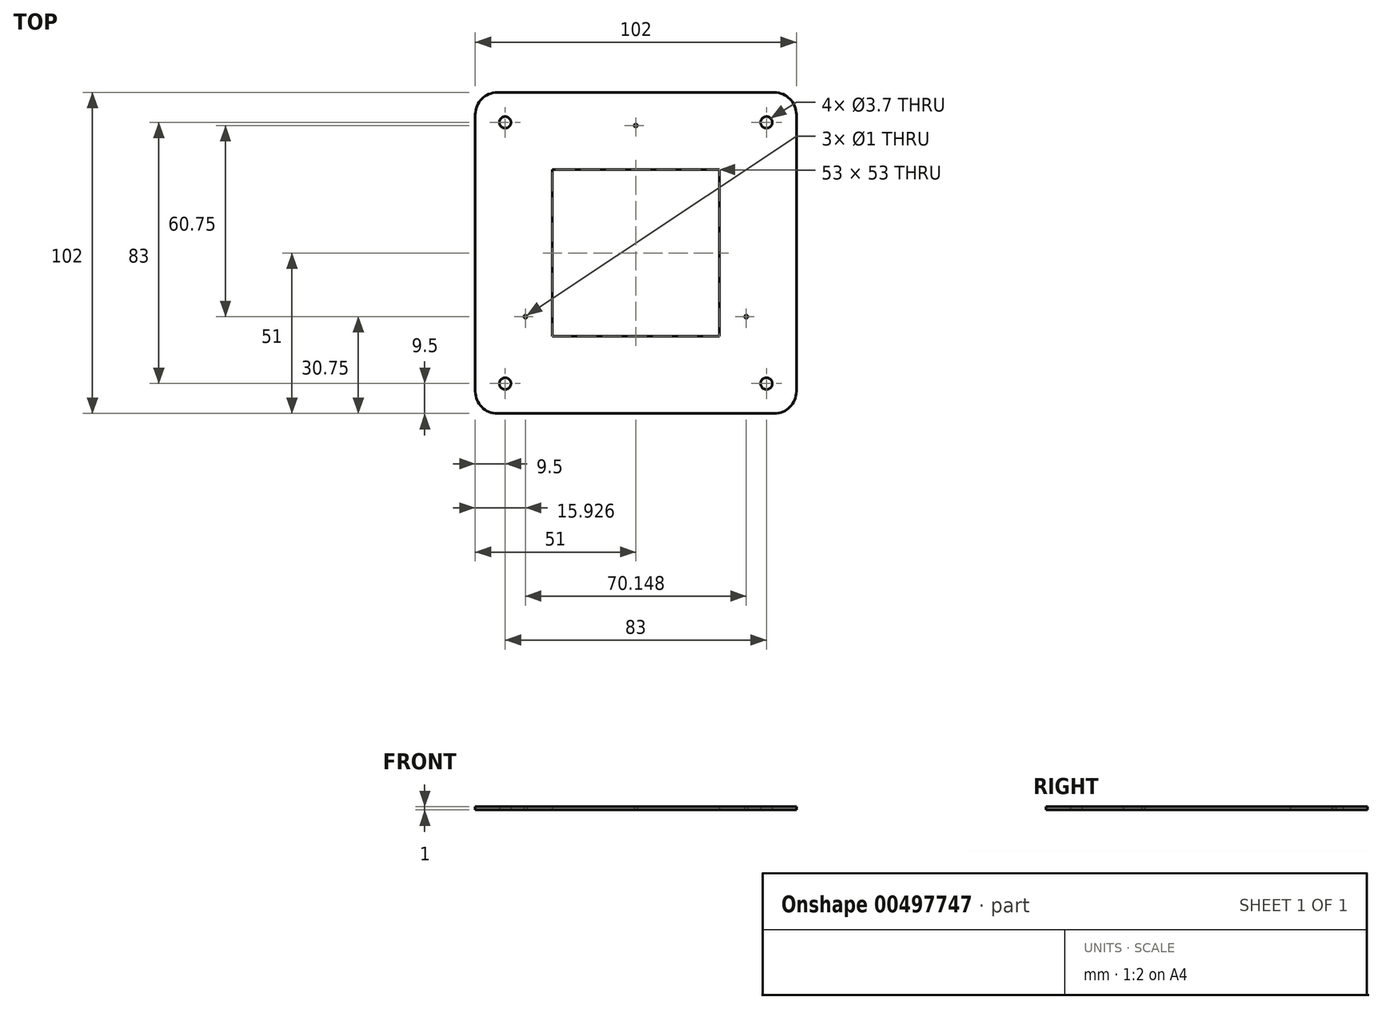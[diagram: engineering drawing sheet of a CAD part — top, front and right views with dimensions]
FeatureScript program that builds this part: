
annotation { "Feature Type Name" : "Feature", "Feature Type Description" : "" }
export const myFeature = defineFeature(function(context is Context, id is Id, definition is map)
    precondition{}
    {
        {
            var Q0;
            Q0=qCreatedBy(makeId("Top.planeOp"),FACE);
            var sketch = newSketch(context, id + "F0", { "sketchPlane" : qUnion([Q0])});
            skCircle(sketch, "E0", {"center": v(0, 0) * mm, "radius": 40.5 * mm, "construction": true});
            skLineSegment(sketch, "E1", {"start": v(0, 40.5) * mm, "end": v(-35.07, -20.25) * mm, "construction": true});
            skLineSegment(sketch, "E2", {"start": v(-35.07, -20.25) * mm, "end": v(35.07, -20.25) * mm, "construction": true});
            skLineSegment(sketch, "E3", {"start": v(35.07, -20.25) * mm, "end": v(0, 40.5) * mm, "construction": true});
            skCircle(sketch, "E4", {"center": v(-35.07, -20.25) * mm, "radius": 0.5 * mm});
            skCircle(sketch, "E5", {"center": v(35.07, -20.25) * mm, "radius": 0.5 * mm});
            skCircle(sketch, "E6", {"center": v(0, 40.5) * mm, "radius": 0.5 * mm});
            skLineSegment(sketch, "E7.bottom", {"start": v(44, -51) * mm, "end": v(-44, -51) * mm});
            skLineSegment(sketch, "E7.top", {"start": v(44, 51) * mm, "end": v(-44, 51) * mm});
            skLineSegment(sketch, "E7.left", {"start": v(51, -44) * mm, "end": v(51, 44) * mm});
            skLineSegment(sketch, "E7.right", {"start": v(-51, -44) * mm, "end": v(-51, 44) * mm});
            skLineSegment(sketch, "E8.bottom", {"start": v(41.5, 41.5) * mm, "end": v(-41.5, 41.5) * mm, "construction": true});
            skLineSegment(sketch, "E8.top", {"start": v(41.5, -41.5) * mm, "end": v(-41.5, -41.5) * mm, "construction": true});
            skLineSegment(sketch, "E8.left", {"start": v(41.5, 41.5) * mm, "end": v(41.5, -41.5) * mm, "construction": true});
            skLineSegment(sketch, "E8.right", {"start": v(-41.5, 41.5) * mm, "end": v(-41.5, -41.5) * mm, "construction": true});
            skCircle(sketch, "E9", {"center": v(-41.5, 41.5) * mm, "radius": 1.85 * mm});
            skCircle(sketch, "E10", {"center": v(41.5, 41.5) * mm, "radius": 1.85 * mm});
            skCircle(sketch, "E11", {"center": v(41.5, -41.5) * mm, "radius": 1.85 * mm});
            skCircle(sketch, "E12", {"center": v(-41.5, -41.5) * mm, "radius": 1.85 * mm});
            skPoint(sketch, "E13.visualSharp", {"position": v(-51, 51) * mm});
            skArc(sketch, "E13.filletArc", {"start": v(-44, 51) * mm, "mid": v(-48.95, 48.95) * mm, "end": v(-51, 44) * mm});
            skPoint(sketch, "E14.visualSharp", {"position": v(51, 51) * mm});
            skArc(sketch, "E14.filletArc", {"start": v(51, 44) * mm, "mid": v(48.95, 48.95) * mm, "end": v(44, 51) * mm});
            skPoint(sketch, "E15.visualSharp", {"position": v(51, -51) * mm});
            skArc(sketch, "E15.filletArc", {"start": v(44, -51) * mm, "mid": v(48.95, -48.95) * mm, "end": v(51, -44) * mm});
            skPoint(sketch, "E16.visualSharp", {"position": v(-51, -51) * mm});
            skArc(sketch, "E16.filletArc", {"start": v(-51, -44) * mm, "mid": v(-48.95, -48.95) * mm, "end": v(-44, -51) * mm});
            skLineSegment(sketch, "E17.bottom", {"start": v(26.5, 26.5) * mm, "end": v(-26.5, 26.5) * mm});
            skLineSegment(sketch, "E17.top", {"start": v(26.5, -26.5) * mm, "end": v(-26.5, -26.5) * mm});
            skLineSegment(sketch, "E17.left", {"start": v(26.5, 26.5) * mm, "end": v(26.5, -26.5) * mm});
            skLineSegment(sketch, "E17.right", {"start": v(-26.5, 26.5) * mm, "end": v(-26.5, -26.5) * mm});
            skSolve(sketch);
        }
        {
            var Q0;
            Q0=makeQuery(id+"F0.imprint","IMPRINT",FACE,{"disambiguationData":[TD([[makeQuery(id+"F0.imprint","IMPRINT",EDGE,{"derivedFrom":sQuery(id+"F0.wireOp",EDGE,"E4")}),-1.0]])]});
            extrude(context, id + "F1", {"entities" : qUnion([Q0]), "depth" : 1 * mm});
        }
    });
